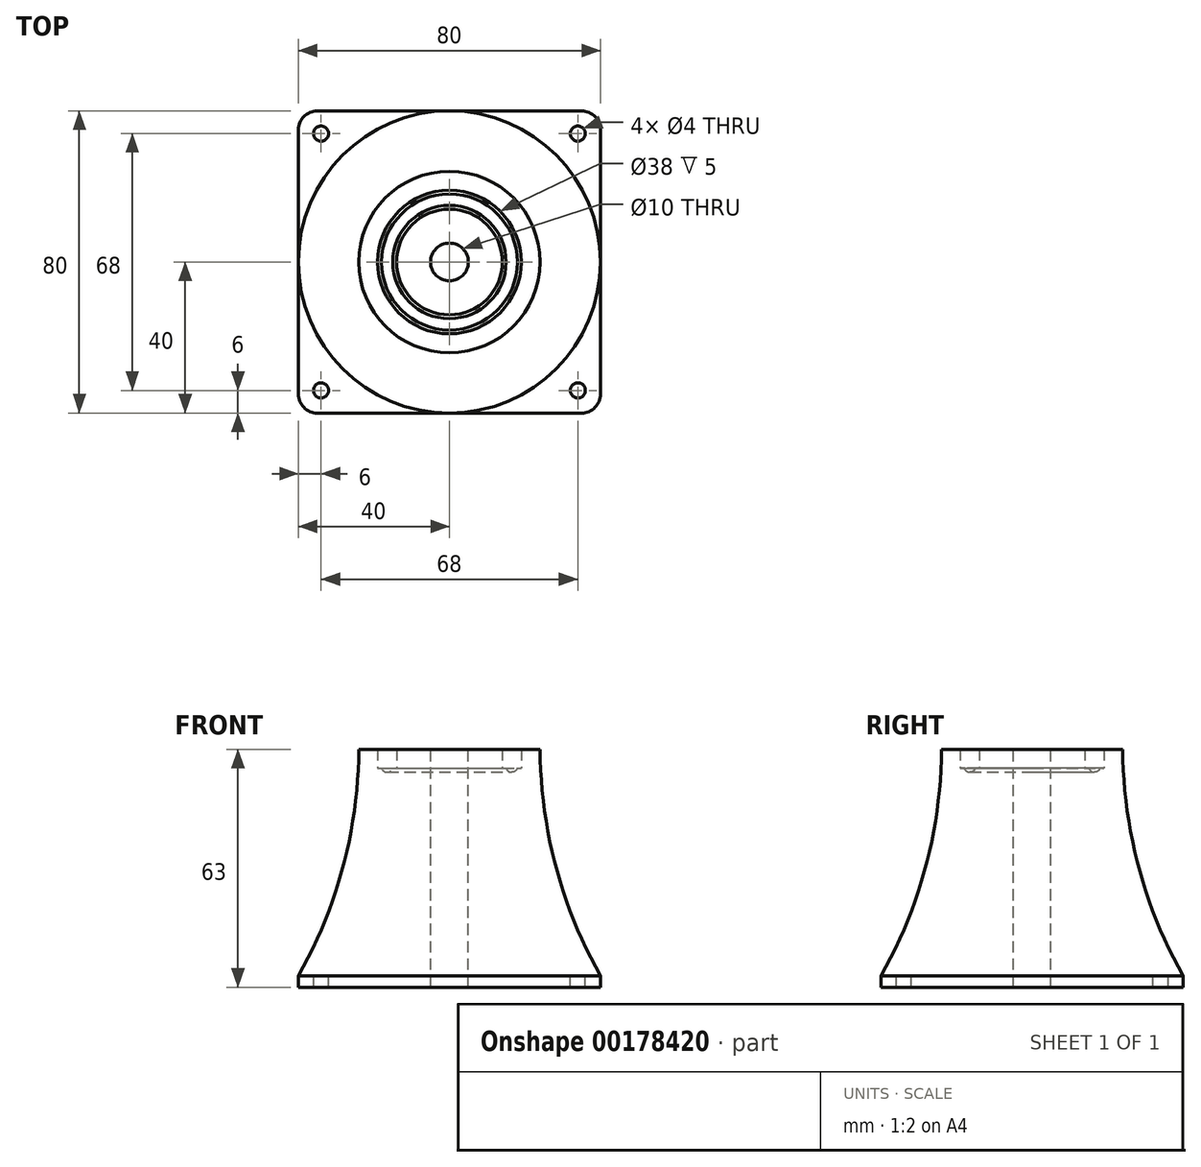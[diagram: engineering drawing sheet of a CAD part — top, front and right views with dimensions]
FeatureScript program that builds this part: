
annotation { "Feature Type Name" : "Feature", "Feature Type Description" : "" }
export const myFeature = defineFeature(function(context is Context, id is Id, definition is map)
    precondition{}
    {
        {
            var Q0;
            Q0=qCreatedBy(makeId("Top.planeOp"),FACE);
            var sketch = newSketch(context, id + "F0", { "sketchPlane" : qUnion([Q0])});
            skLineSegment(sketch, "E0.bottom", {"start": v(0, 0) * mm, "end": v(-40, 0) * mm});
            skLineSegment(sketch, "E0.top", {"start": v(0, 40) * mm, "end": v(-40, 40) * mm});
            skLineSegment(sketch, "E0.left", {"start": v(0, 0) * mm, "end": v(0, 40) * mm});
            skLineSegment(sketch, "E0.right", {"start": v(-40, 0) * mm, "end": v(-40, 40) * mm});
            skSolve(sketch);
        }
        {
            var Q0;
            Q0=makeQuery(id+"F0.imprint","IMPRINT",FACE,{"disambiguationData":[TD([[makeQuery(id+"F0.imprint","IMPRINT",EDGE,{"derivedFrom":sQuery(id+"F0.wireOp",EDGE,"E0.bottom")}),-1.0]])]});
            extrude(context, id + "F1", {"entities" : qUnion([Q0]), "depth" : 3 * mm});
        }
        {
            var Q0;
            Q0=makeQuery(id+"F1.opExtrude","CAP_FACE",FACE,{"disambiguationData":[OSD([sQuery(id+"F0.wireOp",EDGE,"E0.bottom"),sQuery(id+"F0.wireOp",EDGE,"E0.top"),sQuery(id+"F0.wireOp",EDGE,"E0.left"),sQuery(id+"F0.wireOp",EDGE,"E0.right")])],"isStart":false});
            var sketch = newSketch(context, id + "F2", { "sketchPlane" : qUnion([Q0])});
            skPoint(sketch, "E1", {"position": v(-34, 34) * mm});
            skSolve(sketch);
        }
        {
            var Q0;
            Q0=sQuery(id+"F2.wireOp",VERTEX,"E1");
            var Q1;
            Q1=makeQuery(id+"F1.opExtrude","SWEPT_BODY",BODY,{"disambiguationData":[OSD([sQuery(id+"F0.wireOp",EDGE,"E0.bottom"),sQuery(id+"F0.wireOp",EDGE,"E0.top"),sQuery(id+"F0.wireOp",EDGE,"E0.left"),sQuery(id+"F0.wireOp",EDGE,"E0.right")])]});
            hole(context, id + "F3", {"style" : HoleStyle.SIMPLE, "endStyle" : HoleEndStyle.THROUGH, "holeDiameter" : 4 * mm, "locations" : qUnion([Q0]), "scope" : qUnion([Q1]), "isTappedThrough" : true});
        }
        {
            var Q0;
            Q0=makeQuery(id+"F1.opExtrude","SWEPT_EDGE",EDGE,{"disambiguationData":[OSD([sQuery(id+"F0.wireOp",EDGE,"E0.top"),sQuery(id+"F0.wireOp",EDGE,"E0.right")])]});
            fillet(context, id + "F4", {"entities" : qUnion([Q0]), "radius" : 5 * mm, "tangentPropagation" : true, "allowEdgeOverflow" : false});
        }
        {
            var Q0;
            Q0=makeQuery(id+"F1.opExtrude","SWEPT_BODY",BODY,{"disambiguationData":[OSD([sQuery(id+"F0.wireOp",EDGE,"E0.bottom"),sQuery(id+"F0.wireOp",EDGE,"E0.top"),sQuery(id+"F0.wireOp",EDGE,"E0.left"),sQuery(id+"F0.wireOp",EDGE,"E0.right")])]});
            var Q1;
            Q1=makeQuery(id+"F1.opExtrude","SWEPT_FACE",FACE,{"disambiguationData":[OSD([sQuery(id+"F0.wireOp",EDGE,"E0.bottom")])]});
            mirror(context, id + "F5", {"operationType" : NewBodyOperationType.ADD, "entities" : qUnion([Q0]), "mirrorPlane" : qUnion([Q1])});
        }
        {
            var Q0;
            Q0=makeQuery(id+"F1.opExtrude","SWEPT_BODY",BODY,{"disambiguationData":[OSD([sQuery(id+"F0.wireOp",EDGE,"E0.bottom"),sQuery(id+"F0.wireOp",EDGE,"E0.top"),sQuery(id+"F0.wireOp",EDGE,"E0.left"),sQuery(id+"F0.wireOp",EDGE,"E0.right")])]});
            var Q1;
            {var subQ0=makeQuery(id+"F1.opExtrude","SWEPT_FACE",FACE,{"disambiguationData":[OSD([sQuery(id+"F0.wireOp",EDGE,"E0.left")])]});Q1=makeQuery(id+"F5.boolean.opBoolean","MERGE",FACE,{"derivedFrom":[subQ0,makeQuery(id+"F5.opPattern","COPY",FACE,{"derivedFrom":subQ0,"instanceName":"1"})]});}
            mirror(context, id + "F6", {"operationType" : NewBodyOperationType.ADD, "entities" : qUnion([Q0]), "mirrorPlane" : qUnion([Q1])});
        }
        {
            var Q0;
            Q0=qCreatedBy(makeId("Front.planeOp"),FACE);
            var sketch = newSketch(context, id + "F7", { "sketchPlane" : qUnion([Q0])});
            skLineSegment(sketch, "E2", {"start": v(0, 3) * mm, "end": v(0, 63) * mm});
            skLineSegment(sketch, "E3", {"start": v(0, 63) * mm, "end": v(-14, 63) * mm});
            skLineSegment(sketch, "E4", {"start": v(-14, 63) * mm, "end": v(-14, 58) * mm});
            skLineSegment(sketch, "E5", {"start": v(-14, 58) * mm, "end": v(-19, 58) * mm});
            skLineSegment(sketch, "E6", {"start": v(-19, 58) * mm, "end": v(-19, 63) * mm});
            skLineSegment(sketch, "E7", {"start": v(-19, 63) * mm, "end": v(-24, 63) * mm});
            skLineSegment(sketch, "E8", {"start": v(0, 3) * mm, "end": v(-40, 3) * mm});
            skArc(sketch, "E9", {"start": v(-40, 3) * mm, "mid": v(-28.17, 31.98) * mm, "end": v(-24, 63) * mm});
            skArc(sketch, "E10", {"start": v(-18, 58) * mm, "mid": v(-16.5, 56.92) * mm, "end": v(-15, 58) * mm});
            skSolve(sketch);
        }
        {
            var Q0;
            Q0=makeQuery(id+"F7.imprint","IMPRINT",FACE,{"disambiguationData":[TD([[makeQuery(id+"F7.imprint","IMPRINT",EDGE,{"derivedFrom":sQuery(id+"F7.wireOp",EDGE,"E2")}),1.0]])]});
            var Q1;
            Q1=sQuery(id+"F7.wireOp",EDGE,"E2");
            revolve(context, id + "F8", {"operationType" : NewBodyOperationType.ADD, "entities" : qUnion([Q0]), "axis" : qUnion([Q1]), "revolveType" : RevolveType.FULL});
        }
        {
            var Q0;
            Q0=makeQuery(id+"F8.opRevolve","SWEPT_FACE",FACE,{"disambiguationData":[OSD([sQuery(id+"F7.wireOp",EDGE,"E3")])]});
            var sketch = newSketch(context, id + "F9", { "sketchPlane" : qUnion([Q0])});
            skPoint(sketch, "E11", {"position": v(0, 0) * mm});
            skSolve(sketch);
        }
        {
            var Q0;
            Q0=sQuery(id+"F9.wireOp",VERTEX,"E11");
            var Q1;
            Q1=makeQuery(id+"F1.opExtrude","SWEPT_BODY",BODY,{"disambiguationData":[OSD([sQuery(id+"F0.wireOp",EDGE,"E0.bottom"),sQuery(id+"F0.wireOp",EDGE,"E0.top"),sQuery(id+"F0.wireOp",EDGE,"E0.left"),sQuery(id+"F0.wireOp",EDGE,"E0.right")])]});
            hole(context, id + "F10", {"style" : HoleStyle.SIMPLE, "endStyle" : HoleEndStyle.THROUGH, "holeDiameter" : 10 * mm, "locations" : qUnion([Q0]), "scope" : qUnion([Q1]), "isTappedThrough" : true});
        }
    });
